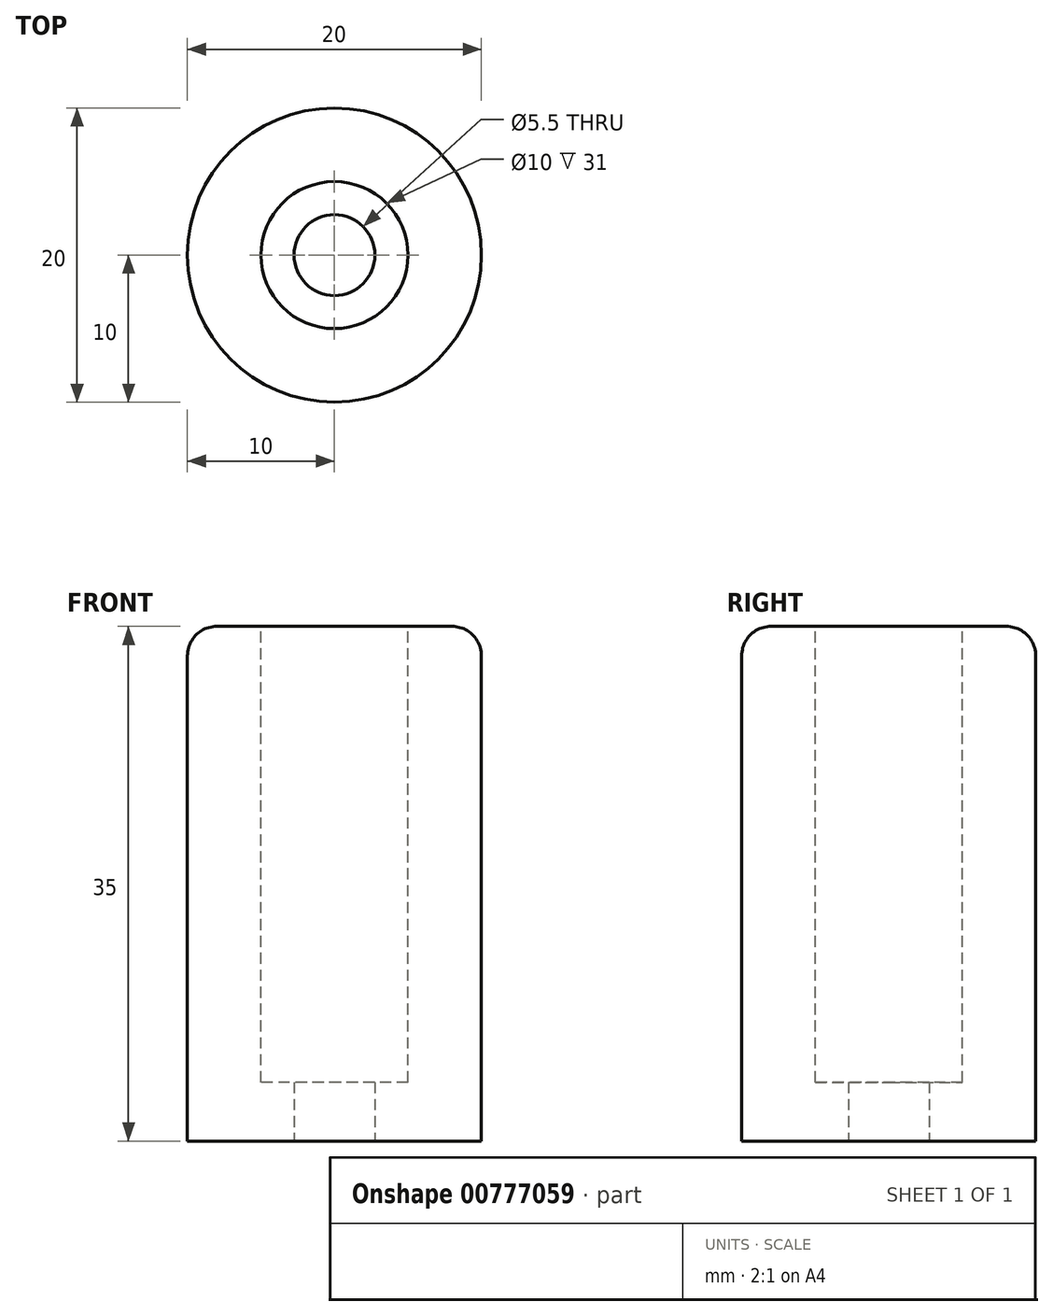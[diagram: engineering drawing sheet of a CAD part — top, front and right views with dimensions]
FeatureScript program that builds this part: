
annotation { "Feature Type Name" : "Feature", "Feature Type Description" : "" }
export const myFeature = defineFeature(function(context is Context, id is Id, definition is map)
    precondition{}
    {
        {
            var Q0;
            Q0=qCreatedBy(makeId("Top.planeOp"),FACE);
            var sketch = newSketch(context, id + "F0", { "sketchPlane" : qUnion([Q0])});
            skCircle(sketch, "E0", {"center": v(0, 0) * mm, "radius": 2.75 * mm});
            skCircle(sketch, "E1", {"center": v(0, 0) * mm, "radius": 10 * mm});
            skSolve(sketch);
        }
        {
            var Q0;
            Q0=qSketchRegion(id+"F0",true);
            extrude(context, id + "F1", {"entities" : qUnion([Q0]), "depth" : 35 * mm, "offsetDistance" : 25 * mm});
        }
        {
            var Q0;
            Q0=makeQuery(id+"F1.opExtrude","CAP_FACE",FACE,{"disambiguationData":[OSD([sQuery(id+"F0.wireOp",EDGE,"E0"),sQuery(id+"F0.wireOp",EDGE,"E1")])],"isStart":false});
            var sketch = newSketch(context, id + "F2", { "sketchPlane" : qUnion([Q0])});
            skCircle(sketch, "E2.0", {"center": v(0, 0) * mm, "radius": 2.75 * mm});
            skCircle(sketch, "E3", {"center": v(0, 0) * mm, "radius": 5 * mm});
            skSolve(sketch);
        }
        {
            var Q0;
            Q0=qSketchRegion(id+"F2",true);
            extrude(context, id + "F3", {"entities" : qUnion([Q0]), "operationType" : NewBodyOperationType.REMOVE, "oppositeDirection" : true, "depth" : 31 * mm, "offsetDistance" : 25 * mm});
        }
        {
            var Q0;
            Q0=makeQuery(id+"F3.boolean.opBoolean","COPY",EDGE,{"derivedFrom":makeQuery(id+"F3.opExtrude","CAP_EDGE",EDGE,{"disambiguationData":[OSD([sQuery(id+"F2.wireOp",EDGE,"E3")])],"isStart":true})});
            var Q1;
            Q1=makeQuery(id+"F1.opExtrude","CAP_EDGE",EDGE,{"disambiguationData":[OSD([sQuery(id+"F0.wireOp",EDGE,"E1")])],"isStart":false});
            fillet(context, id + "F4", {"entities" : qUnion([Q0, Q1]), "radius" : 2 * mm, "tangentPropagation" : true, "allowEdgeOverflow" : false});
        }
    });
